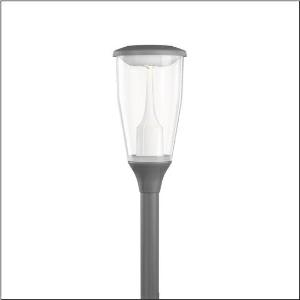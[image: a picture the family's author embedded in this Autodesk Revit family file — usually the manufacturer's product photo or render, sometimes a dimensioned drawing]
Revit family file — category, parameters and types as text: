
# Revit family: dl_11_iq___p1_0a_5xa5565ff14h000022_0ce9
name_source: partatom
category: Lighting Fixtures
units: mm (PartAtom-declared; Revit-internal decimal feet)

## family parameters
Cut with Voids When Loaded = No
Host = Face
Light Source = No
Part Type = Normal
Room Calculation Point = No
Round Connector Dimension = Use Diameter
Shared = No

## types (1)
- --- (1 x LED, 1530 lm, 10.5 W, 3000K)
    Apparent Load = 11 VA
    CIE Flux Codes = 34 63 91 95 100
    Color Rendering = 70
    Color Temperature = 3000K
    Default Elevation = 1800 mm
    Description = DL 11 iQ, mast luminaire, Module 540 iQ-SR, primary light control with 3 zone facetted reflector, of plastic, silver coated, highly specular, structured, primary optical cover: cover, of PMMA, transparent, light distribution: P1.0a, light emission: direct distribution, primary light characteristic: asymmetric, installation type: post-top, LED, High Power LED, rated luminous flux: 1.560lm, luminous efficacy: 149lm/W, light colour: 730, colour temperature: 3000K, control: Street-Remote, Auto-Match, Temp-Guard, Lumen-Switch, Night-Set, Smart-Wire, Light-Fading, Desk-Remote (wireless, voltage-free reading and setting of iQ features in the workshop via application-optimized NFC function/RFID function), optimised constant luminous flux control (CLO 2.0), mains connection: 220..240V, AC, 50/60Hz, connection cable pre-assembled, cable length: 5,5m, start of lifetime: 10W, end of service life: 11W, reduction: 5W, luminaire housing, upper part, of diecast aluminium, coated, Siteco® metallic grey (DB 702S), spigot size: 60mm (post-top), post-top mast mounting element, of diecast aluminium, coated, Siteco® metallic grey (DB 702S), Module 540 iQ-SR, traffic white (RAL 9016), equipment: standard, protection rating (complete): IP66, insulation class (complete): insulation class II (safety insulation), certification: CE, ENEC, ENEC+, VDE, packaging unit: 1 piece

Light Distribution: P1.0a
    Height = 665 mm
    Lamp = 1 x LED
    Lamp Light Flux = 1530 lm
    Lamp Power = 10.5 W
    Lamp count = 1
    Length = 334 mm
    Luminous efficacy = 146 lm/W
    Manufacturer = Siteco
    ModVariant = No
    Model = 5XA5565FF14H000022
    Number of Poles = 1
    OnlyDefault = Yes
    Power Factor = 1
    Product Name = DL 11 iQ | P1.0a
    Product group = mast luminaire | pylon top
    ProductGroupID = 6100
    Protection Class = Protection class II
    Protection Degree = IP 66
    RLX_Detail_Level = 1
    RLX_Emergency_Light_Flux = 0 lm
    RLX_Emergency_Type = 0
    RLX_Emergency_Type_DB = No
    RlxData = <blob elided: 104477 chars, md5=d351ec66>
    Socket = socket
    Standby Power = 0 W
    System Light Flux = 1530 lm
    System Power = 11 W
    Type Comments = factory setting: luminous flux: 100 % | dim-lin: 254 | 419 mA
    Type Image = l_1258354.jpg
    URL = http://relux.com
    VarID = @adj_024279
    Voltage = 0 V
    Weight = 0.00 kg
    Width = 0 mm  [stored 0 ft]

note: [stored X ft] marks values corroborated as IEEE doubles in the binary element streams (Revit-internal decimal feet)

## geometry (parser evidence)
native form markers: Blend x4, Sweep x10
no freeform markers — native parametric forms only
